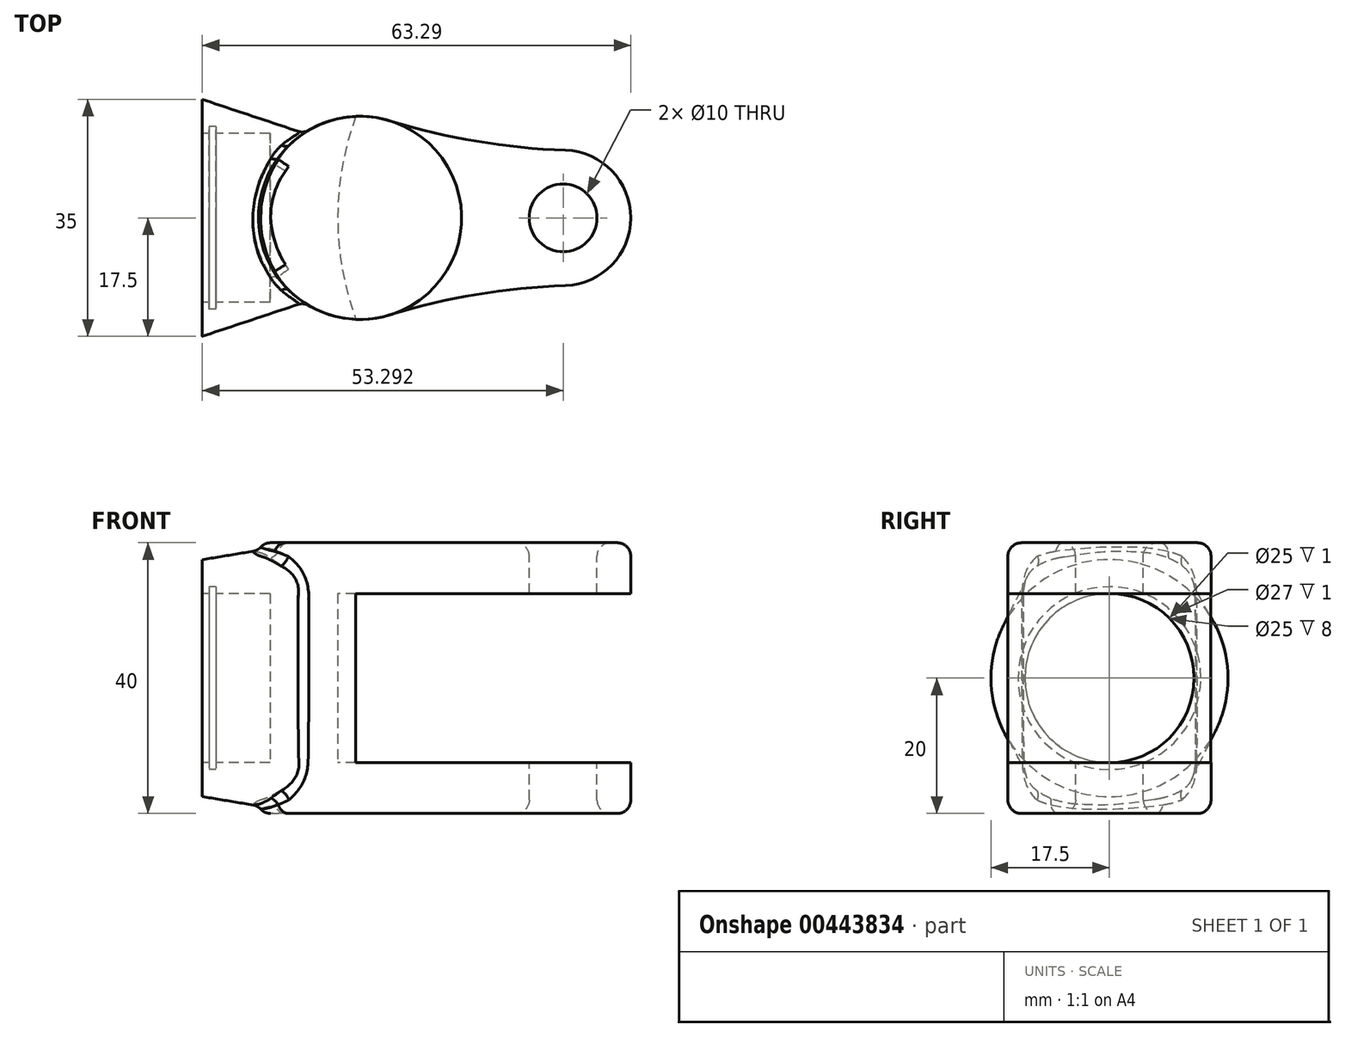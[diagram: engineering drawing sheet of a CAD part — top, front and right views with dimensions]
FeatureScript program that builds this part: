
annotation { "Feature Type Name" : "Feature", "Feature Type Description" : "" }
export const myFeature = defineFeature(function(context is Context, id is Id, definition is map)
    precondition{}
    {
        {
            var Q0;
            Q0=qCreatedBy(makeId("Right.planeOp"),FACE);
            var sketch = newSketch(context, id + "F0", { "sketchPlane" : qUnion([Q0])});
            skCircle(sketch, "E0", {"center": v(0, 0) * mm, "radius": 17.5 * mm});
            skSolve(sketch);
        }
        {
            var Q0;
            Q0=qCreatedBy(makeId("Right.planeOp"),FACE);
            cPlane(context, id + "F1", {"entities" : qUnion([Q0]), "cplaneType" : CPlaneType.OFFSET, "offset" : 15 * mm, "width" : 150 * mm, "height" : 150 * mm});
        }
        {
            var Q0;
            Q0=qCreatedBy(id+"F1.planeOp",FACE);
            var sketch = newSketch(context, id + "F2", { "sketchPlane" : qUnion([Q0])});
            skLineSegment(sketch, "E1.bottom", {"start": v(5, 20) * mm, "end": v(-5, 20) * mm});
            skLineSegment(sketch, "E1.top", {"start": v(5, -20) * mm, "end": v(-5, -20) * mm});
            skLineSegment(sketch, "E1.left", {"start": v(12.5, 12.5) * mm, "end": v(12.5, -12.5) * mm});
            skLineSegment(sketch, "E1.right", {"start": v(-12.5, 12.5) * mm, "end": v(-12.5, -12.5) * mm});
            skPoint(sketch, "E1.middle", {"position": v(0, 0) * mm});
            skPoint(sketch, "E2.visualSharp", {"position": v(-12.5, 20) * mm});
            skArc(sketch, "E2.filletArc", {"start": v(-5, 20) * mm, "mid": v(-10.3, 17.8) * mm, "end": v(-12.5, 12.5) * mm});
            skPoint(sketch, "E3.visualSharp", {"position": v(12.5, 20) * mm});
            skArc(sketch, "E3.filletArc", {"start": v(12.5, 12.5) * mm, "mid": v(10.3, 17.8) * mm, "end": v(5, 20) * mm});
            skPoint(sketch, "E4.visualSharp", {"position": v(12.5, -20) * mm});
            skArc(sketch, "E4.filletArc", {"start": v(5, -20) * mm, "mid": v(10.3, -17.8) * mm, "end": v(12.5, -12.5) * mm});
            skPoint(sketch, "E5.visualSharp", {"position": v(-12.5, -20) * mm});
            skArc(sketch, "E5.filletArc", {"start": v(-12.5, -12.5) * mm, "mid": v(-10.3, -17.8) * mm, "end": v(-5, -20) * mm});
            skSolve(sketch);
        }
        {
            var Q0;
            Q0=makeQuery(id+"F0.imprint","IMPRINT",FACE,{"disambiguationData":[TD([[makeQuery(id+"F0.imprint","IMPRINT",EDGE,{"derivedFrom":sQuery(id+"F0.wireOp",EDGE,"E0")}),1.0]])]});
            var Q1;
            Q1=makeQuery(id+"F2.imprint","IMPRINT",FACE,{"disambiguationData":[TD([[makeQuery(id+"F2.imprint","IMPRINT",EDGE,{"derivedFrom":sQuery(id+"F2.wireOp",EDGE,"E1.bottom")}),1.0]])]});
            loft(context, id + "F3", {"sheetProfilesArray" : [{ "sheetProfileEntities" : qUnion([Q0]) }, { "sheetProfileEntities" : qUnion([Q1]) }]});
        }
        {
            var Q0;
            Q0=qCreatedBy(makeId("Top.planeOp"),FACE);
            var sketch = newSketch(context, id + "F4", { "sketchPlane" : qUnion([Q0])});
            skArc(sketch, "E6", {"start": v(27.7, 14.34) * mm, "mid": v(8.3, 0) * mm, "end": v(27.7, -14.34) * mm});
            skArc(sketch, "E7", {"start": v(53.63, -10) * mm, "mid": v(63.3, 0) * mm, "end": v(53.63, 10) * mm});
            skArc(sketch, "E8", {"start": v(53.63, -10) * mm, "mid": v(40.52, -11.31) * mm, "end": v(27.7, -14.34) * mm});
            skArc(sketch, "E9", {"start": v(27.7, 14.34) * mm, "mid": v(40.52, 11.31) * mm, "end": v(53.63, 10) * mm});
            skSolve(sketch);
        }
        {
            var Q0;
            Q0 = qSketchRegion(id + "F4", true);
            extrude(context, id + "F5", {"entities" : qUnion([Q0]), "operationType" : NewBodyOperationType.ADD, "endBound" : BoundingType.SYMMETRIC, "depth" : 40 * mm});
        }
        {
            var Q0;
            Q0=qCreatedBy(makeId("Front.planeOp"),FACE);
            var sketch = newSketch(context, id + "F6", { "sketchPlane" : qUnion([Q0])});
            skLineSegment(sketch, "E10.bottom", {"start": v(20, 12.5) * mm, "end": v(63.3, 12.5) * mm});
            skLineSegment(sketch, "E10.top", {"start": v(20, -12.5) * mm, "end": v(63.3, -12.5) * mm});
            skLineSegment(sketch, "E10.left", {"start": v(20, 12.5) * mm, "end": v(20, -12.5) * mm});
            skLineSegment(sketch, "E10.right", {"start": v(63.3, 12.5) * mm, "end": v(63.3, -12.5) * mm});
            skSolve(sketch);
        }
        {
            var Q0;
            Q0 = qSketchRegion(id + "F6", true);
            var Q1;
            Q1=sQuery(id+"F6.wireOp",EDGE,"E10.right");
            revolve(context, id + "F7", {"operationType" : NewBodyOperationType.REMOVE, "entities" : qUnion([Q0]), "axis" : qUnion([Q1]), "revolveType" : RevolveType.FULL, "oppositeDirection" : true});
        }
        {
            var Q0;
            Q0=makeQuery(id+"F3.opLoft","CAP_FACE",FACE,{"disambiguationData":[OSD([makeQuery(id+"F0.imprint","IMPRINT",FACE,{"disambiguationData":[TD([[makeQuery(id+"F0.imprint","IMPRINT",EDGE,{"derivedFrom":sQuery(id+"F0.wireOp",EDGE,"E0")}),1.0]])]})])],"isStart":true});
            var sketch = newSketch(context, id + "F8", { "sketchPlane" : qUnion([Q0])});
            skCircle(sketch, "E11", {"center": v(0, 0) * mm, "radius": 12.5 * mm});
            skSolve(sketch);
        }
        {
            var Q0;
            Q0 = qSketchRegion(id + "F8", true);
            extrude(context, id + "F9", {"entities" : qUnion([Q0]), "operationType" : NewBodyOperationType.REMOVE, "oppositeDirection" : true, "depth" : 10 * mm});
        }
        {
            var Q0;
            Q0=makeQuery(id+"F3.opLoft","CAP_FACE",FACE,{"disambiguationData":[OSD([makeQuery(id+"F0.imprint","IMPRINT",FACE,{"disambiguationData":[TD([[makeQuery(id+"F0.imprint","IMPRINT",EDGE,{"derivedFrom":sQuery(id+"F0.wireOp",EDGE,"E0")}),1.0]])]})])],"isStart":true});
            cPlane(context, id + "F10", {"entities" : qUnion([Q0]), "cplaneType" : CPlaneType.OFFSET, "offset" : 1 * mm, "oppositeDirection" : true, "width" : 150 * mm, "height" : 150 * mm});
        }
        {
            var Q0;
            Q0=qCreatedBy(id+"F10.planeOp",FACE);
            var sketch = newSketch(context, id + "F11", { "sketchPlane" : qUnion([Q0])});
            skCircle(sketch, "E12.0", {"center": v(0, 0) * mm, "radius": 13.5 * mm});
            skSolve(sketch);
        }
        {
            var Q0;
            Q0 = qSketchRegion(id + "F11", true);
            extrude(context, id + "F12", {"entities" : qUnion([Q0]), "operationType" : NewBodyOperationType.REMOVE, "oppositeDirection" : true, "depth" : 1 * mm});
        }
        {
            var Q0;
            Q0=makeQuery(id+"F5.opExtrude","CAP_FACE",FACE,{"disambiguationData":[OSD([sQuery(id+"F4.wireOp",EDGE,"E6"),sQuery(id+"F4.wireOp",EDGE,"E7"),sQuery(id+"F4.wireOp",EDGE,"E8"),sQuery(id+"F4.wireOp",EDGE,"E9")])],"isStart":false});
            var sketch = newSketch(context, id + "F13", { "sketchPlane" : qUnion([Q0])});
            skCircle(sketch, "E13", {"center": v(53.3, 0) * mm, "radius": 5 * mm});
            skSolve(sketch);
        }
        {
            var Q0;
            Q0 = qSketchRegion(id + "F13", true);
            extrude(context, id + "F14", {"entities" : qUnion([Q0]), "operationType" : NewBodyOperationType.REMOVE, "endBound" : BoundingType.THROUGH_ALL, "oppositeDirection" : true, "depth" : 25 * mm});
        }
        {
            var Q0;
            Q0=makeQuery(id+"F5.opExtrude","CAP_FACE",FACE,{"disambiguationData":[OSD([sQuery(id+"F4.wireOp",EDGE,"E6"),sQuery(id+"F4.wireOp",EDGE,"E7"),sQuery(id+"F4.wireOp",EDGE,"E8"),sQuery(id+"F4.wireOp",EDGE,"E9")])],"isStart":true});
            var Q1;
            Q1=makeQuery(id+"F5.opExtrude","CAP_FACE",FACE,{"disambiguationData":[OSD([sQuery(id+"F4.wireOp",EDGE,"E6"),sQuery(id+"F4.wireOp",EDGE,"E7"),sQuery(id+"F4.wireOp",EDGE,"E8"),sQuery(id+"F4.wireOp",EDGE,"E9")])],"isStart":false});
            fillet(context, id + "F15", {"entities" : qUnion([Q0, Q1]), "radius" : 2 * mm, "tangentPropagation" : true, "allowEdgeOverflow" : false});
        }
        {
            var Q0;
            Q0=makeQuery(id+"F15.opFillet","BLEND_EDGE",EDGE,{"blendedFrom":[makeQuery(id+"F5.opExtrude","CAP_EDGE",EDGE,{"disambiguationData":[OSD([sQuery(id+"F4.wireOp",EDGE,"E6")])],"isStart":false}),makeQuery(id+"F3.opLoft","SWEPT_FACE",FACE,{"disambiguationData":[OSD([sQuery(id+"F0.wireOp",EDGE,"E0"),sQuery(id+"F2.wireOp",EDGE,"E1.bottom"),sQuery(id+"F2.wireOp",EDGE,"E2.filletArc"),sQuery(id+"F2.wireOp",EDGE,"E3.filletArc")])]})],"blendedInto":[makeQuery(id+"F3.opLoft","SWEPT_FACE",FACE,{"disambiguationData":[OSD([sQuery(id+"F0.wireOp",EDGE,"E0"),sQuery(id+"F2.wireOp",EDGE,"E1.bottom"),sQuery(id+"F2.wireOp",EDGE,"E2.filletArc"),sQuery(id+"F2.wireOp",EDGE,"E3.filletArc")])]})]});
            var Q1;
            Q1=makeQuery(id+"F5.boolean.opBoolean","INTERSECT",EDGE,{"disambiguationData":[OD(0.0)],"derivedFrom":[makeQuery(id+"F3.opLoft","SWEPT_FACE",FACE,{"disambiguationData":[OSD([sQuery(id+"F0.wireOp",EDGE,"E0"),sQuery(id+"F2.wireOp",EDGE,"E1.bottom"),sQuery(id+"F2.wireOp",EDGE,"E2.filletArc"),sQuery(id+"F2.wireOp",EDGE,"E3.filletArc")])]}),makeQuery(id+"F5.opExtrude","SWEPT_FACE",FACE,{"disambiguationData":[OSD([sQuery(id+"F4.wireOp",EDGE,"E6")])]})]});
            var Q2;
            Q2=makeQuery(id+"F3.opLoft","MID_CAP_EDGE",EDGE,{"disambiguationData":[OSD([sQuery(id+"F2.wireOp",EDGE,"E1.right"),sQuery(id+"F2.wireOp",EDGE,"E2.filletArc"),sQuery(id+"F2.wireOp",EDGE,"E5.filletArc")])],"capPos":1.0});
            var Q3;
            Q3=makeQuery(id+"F5.boolean.opBoolean","INTERSECT",EDGE,{"disambiguationData":[OD(1.0)],"derivedFrom":[makeQuery(id+"F3.opLoft","SWEPT_FACE",FACE,{"disambiguationData":[OSD([sQuery(id+"F0.wireOp",EDGE,"E0"),sQuery(id+"F2.wireOp",EDGE,"E1.bottom"),sQuery(id+"F2.wireOp",EDGE,"E2.filletArc"),sQuery(id+"F2.wireOp",EDGE,"E3.filletArc")])]}),makeQuery(id+"F5.opExtrude","SWEPT_FACE",FACE,{"disambiguationData":[OSD([sQuery(id+"F4.wireOp",EDGE,"E6")])]})]});
            var Q4;
            Q4=makeQuery(id+"F15.opFillet","BLEND_EDGE",EDGE,{"blendedFrom":[makeQuery(id+"F5.opExtrude","CAP_EDGE",EDGE,{"disambiguationData":[OSD([sQuery(id+"F4.wireOp",EDGE,"E6")])],"isStart":true}),makeQuery(id+"F3.opLoft","SWEPT_FACE",FACE,{"disambiguationData":[OSD([sQuery(id+"F0.wireOp",EDGE,"E0"),sQuery(id+"F2.wireOp",EDGE,"E1.bottom"),sQuery(id+"F2.wireOp",EDGE,"E2.filletArc"),sQuery(id+"F2.wireOp",EDGE,"E3.filletArc")])]})],"blendedInto":[makeQuery(id+"F3.opLoft","SWEPT_FACE",FACE,{"disambiguationData":[OSD([sQuery(id+"F0.wireOp",EDGE,"E0"),sQuery(id+"F2.wireOp",EDGE,"E1.bottom"),sQuery(id+"F2.wireOp",EDGE,"E2.filletArc"),sQuery(id+"F2.wireOp",EDGE,"E3.filletArc")])]})]});
            var Q5;
            Q5=makeQuery(id+"F3.opLoft","MID_CAP_EDGE",EDGE,{"disambiguationData":[OSD([sQuery(id+"F2.wireOp",EDGE,"E1.left"),sQuery(id+"F2.wireOp",EDGE,"E3.filletArc"),sQuery(id+"F2.wireOp",EDGE,"E4.filletArc")])],"capPos":1.0});
            fillet(context, id + "F16", {"entities" : qUnion([Q0, Q1, Q2, Q3, Q4, Q5]), "radius" : 2 * mm, "tangentPropagation" : true, "allowEdgeOverflow" : false});
        }
    });
